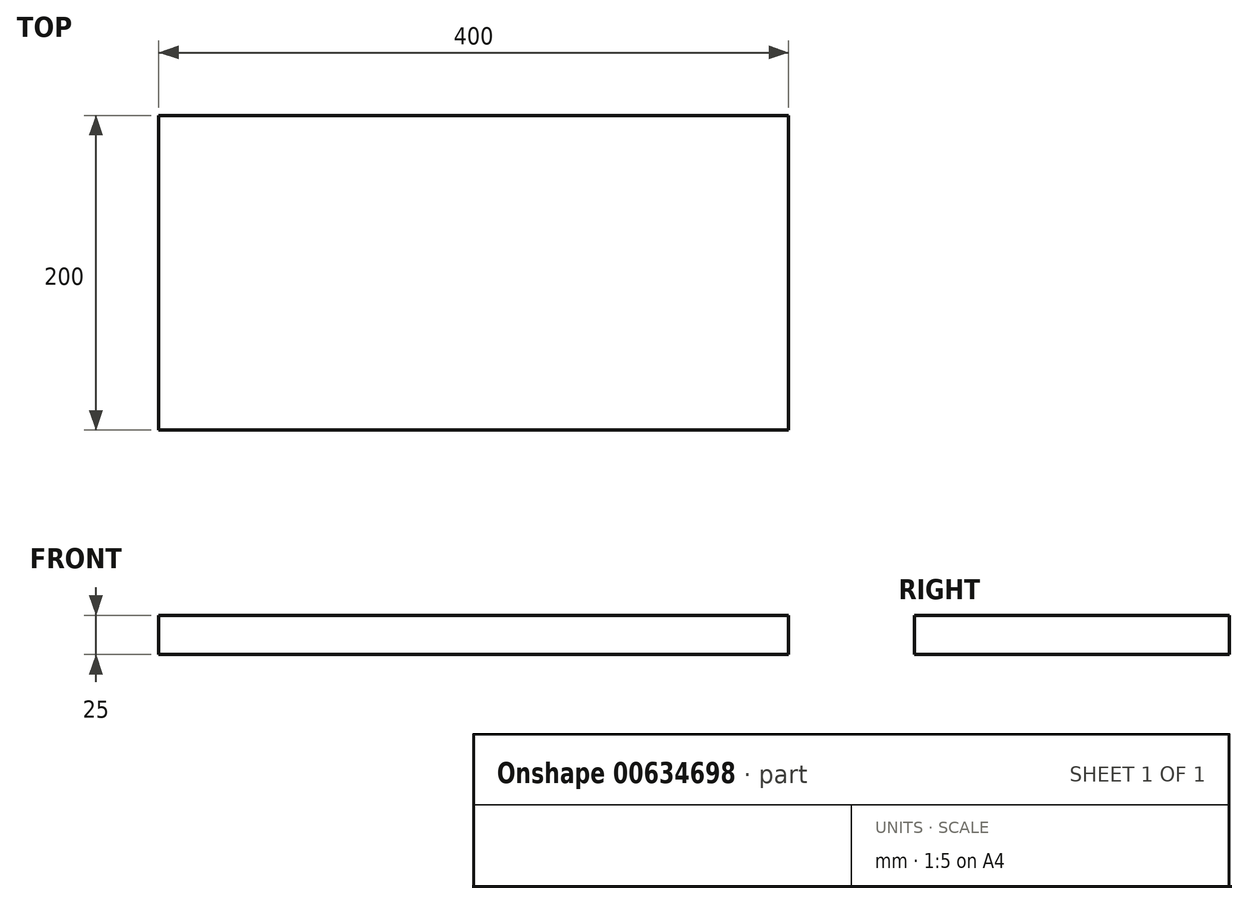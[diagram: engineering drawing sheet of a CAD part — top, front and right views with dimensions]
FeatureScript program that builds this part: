
annotation { "Feature Type Name" : "Feature", "Feature Type Description" : "" }
export const myFeature = defineFeature(function(context is Context, id is Id, definition is map)
    precondition{}
    {
        {
            var Q0;
            Q0=qCreatedBy(makeId("Top.planeOp"),FACE);
            var sketch = newSketch(context, id + "F0", { "sketchPlane" : qUnion([Q0])});
            skLineSegment(sketch, "E0.bottom", {"start": v(0, 0) * mm, "end": v(400, 0) * mm});
            skLineSegment(sketch, "E0.top", {"start": v(0, -200) * mm, "end": v(400, -200) * mm});
            skLineSegment(sketch, "E0.left", {"start": v(0, 0) * mm, "end": v(0, -200) * mm});
            skLineSegment(sketch, "E0.right", {"start": v(400, 0) * mm, "end": v(400, -200) * mm});
            skSolve(sketch);
        }
        {
            var Q0;
            Q0 = qSketchRegion(id + "F0", true);
            extrude(context, id + "F1", {"entities" : qUnion([Q0]), "depth" : 25 * mm, "offsetDistance" : 25 * mm});
        }
    });
